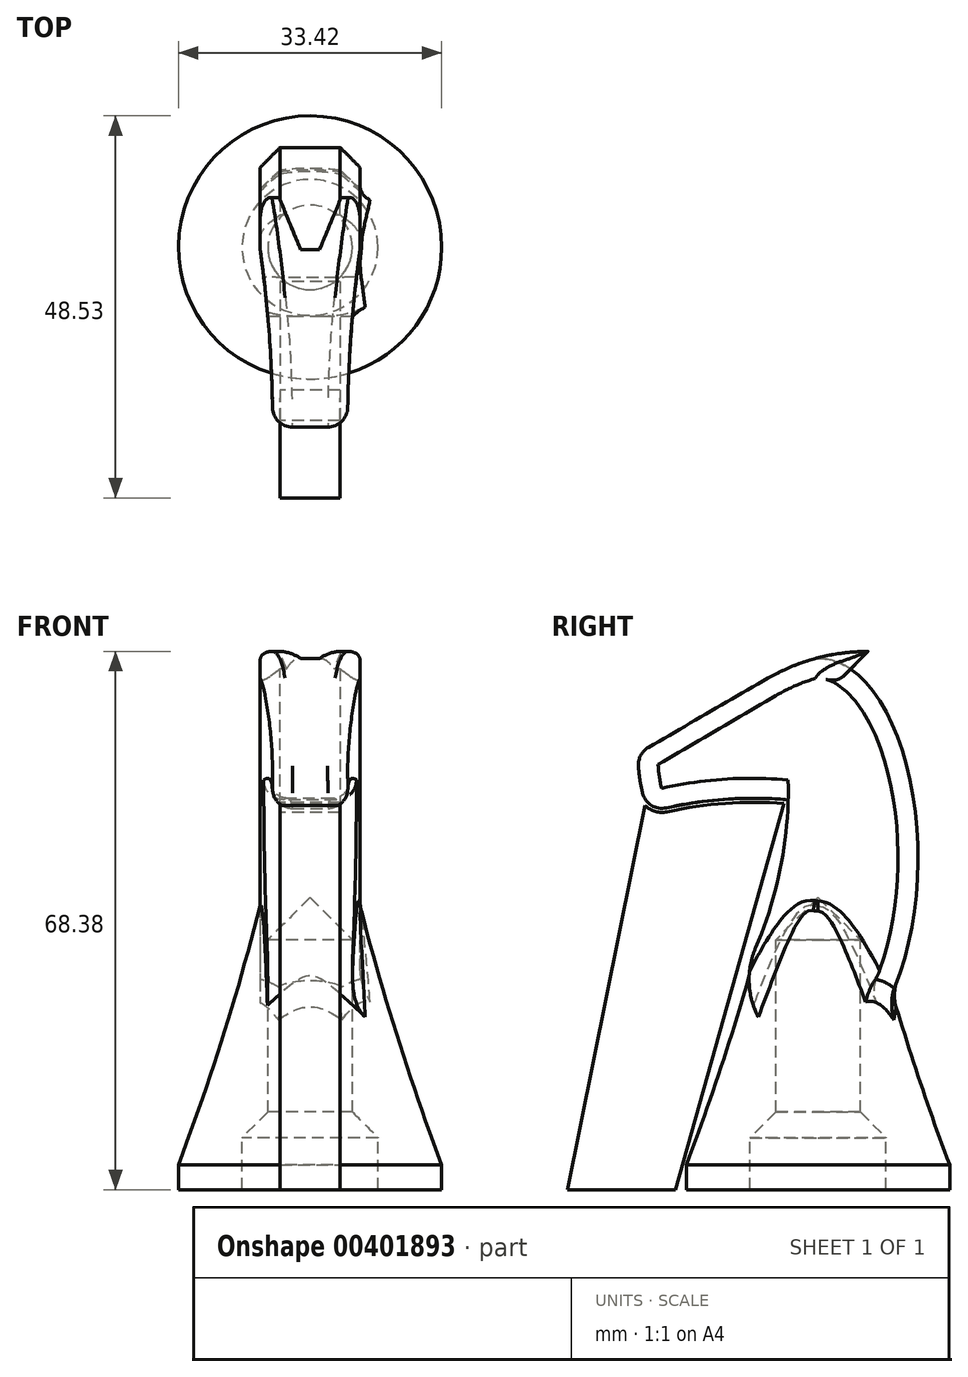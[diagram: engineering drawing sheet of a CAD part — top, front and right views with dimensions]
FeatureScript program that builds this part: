
annotation { "Feature Type Name" : "Feature", "Feature Type Description" : "" }
export const myFeature = defineFeature(function(context is Context, id is Id, definition is map)
    precondition{}
    {
        {
            var Q0;
            Q0=qCreatedBy(makeId("Right.planeOp"),FACE);
            var sketch = newSketch(context, id + "F0", { "sketchPlane" : qUnion([Q0])});
            skArc(sketch, "E0", {"start": v(6.35, 68.38) * mm, "mid": v(-0.22, 67.51) * mm, "end": v(-6.35, 64.97) * mm});
            skLineSegment(sketch, "E1.bottom", {"start": v(-16.71, 68.38) * mm, "end": v(16.71, 68.38) * mm, "construction": true});
            skLineSegment(sketch, "E1.top", {"start": v(-16.71, 0) * mm, "end": v(16.71, 0) * mm, "construction": true});
            skLineSegment(sketch, "E1.left", {"start": v(-16.71, 68.38) * mm, "end": v(-16.71, 0) * mm, "construction": true});
            skLineSegment(sketch, "E1.right", {"start": v(16.71, 68.38) * mm, "end": v(16.71, 0) * mm, "construction": true});
            skArc(sketch, "E2", {"start": v(-22.85, 55.45) * mm, "mid": v(-22.57, 51.63) * mm, "end": v(-21.52, 47.94) * mm});
            skLineSegment(sketch, "E3", {"start": v(-22.85, 55.45) * mm, "end": v(-6.35, 64.97) * mm});
            skLineSegment(sketch, "E4", {"start": v(-3.8, 54.94) * mm, "end": v(-22.57, 51.63) * mm, "construction": true});
            skLineSegment(sketch, "E5", {"start": v(6.35, 68.38) * mm, "end": v(4.1, 66.13) * mm});
            skArc(sketch, "E6", {"start": v(-3.8, 49.53) * mm, "mid": v(-12.74, 49.52) * mm, "end": v(-21.52, 47.94) * mm});
            skArc(sketch, "E7", {"start": v(-7.94, 30.7) * mm, "mid": v(-4.97, 39.92) * mm, "end": v(-3.81, 49.53) * mm});
            skEllipticalArc(sketch, "E8", {});
            skPoint(sketch, "E9.visualSharp", {"position": v(-10, 26.46) * mm});
            skArc(sketch, "E9.filletArc", {"start": v(-7.94, 30.7) * mm, "mid": v(-7.62, 21.98) * mm, "end": v(-0.66, 16.73) * mm});
            const initialGuessF0  = {"E8": [0, 0.04209513881585966, 0, 1, 0.0254, 0.0127, 3.089740436383142, 5.954051655491451]};
            skSetInitialGuess(sketch, initialGuessF0);
            skSolve(sketch);
        }
        {
            var Q0;
            Q0 = qSketchRegion(id + "F0", true);
            extrude(context, id + "F1", {"entities" : qUnion([Q0]), "depth" : 12.7 * mm, "symmetric" : true});
        }
        {
            var Q0;
            Q0=qCreatedBy(makeId("Top.planeOp"),FACE);
            var sketch = newSketch(context, id + "F2", { "sketchPlane" : qUnion([Q0])});
            skCircle(sketch, "E10", {"center": v(166.76, -22.85) * mm, "radius": 162 * mm});
            skLineSegment(sketch, "E11", {"start": v(0, 0) * mm, "end": v(0, 17.42) * mm, "construction": true});
            skCircle(sketch, "E12.MirrorC", {"center": v(-166.76, -22.85) * mm, "radius": 162 * mm});
            skSolve(sketch);
        }
        {
            var Q0;
            Q0 = qSketchRegion(id + "F2", true);
            extrude(context, id + "F3", {"entities" : qUnion([Q0]), "operationType" : NewBodyOperationType.REMOVE, "endBound" : BoundingType.THROUGH_ALL, "depth" : 25.4 * mm});
        }
        {
            var Q0;
            Q0=qCreatedBy(makeId("Right.planeOp"),FACE);
            var sketch = newSketch(context, id + "F4", { "sketchPlane" : qUnion([Q0])});
            skLineSegment(sketch, "E13", {"start": v(-8.64, 0) * mm, "end": v(-16.71, 0) * mm});
            skLineSegment(sketch, "E14", {"start": v(-16.71, 0) * mm, "end": v(-16.71, 3.17) * mm});
            skArc(sketch, "E15", {"start": v(-16.71, 3.17) * mm, "mid": v(-6.63, 34.92) * mm, "end": v(0, 67.57) * mm});
            skLineSegment(sketch, "E16", {"start": v(0, 67.57) * mm, "end": v(0, 37.12) * mm});
            skLineSegment(sketch, "E17", {"start": v(0, 37.12) * mm, "end": v(-5.37, 31.75) * mm});
            skLineSegment(sketch, "E18", {"start": v(-5.37, 31.75) * mm, "end": v(-5.37, 9.87) * mm});
            skLineSegment(sketch, "E19", {"start": v(-5.37, 9.87) * mm, "end": v(-8.64, 6.6) * mm});
            skLineSegment(sketch, "E20", {"start": v(-8.64, 6.6) * mm, "end": v(-8.64, 0) * mm});
            skSolve(sketch);
        }
        {
            var Q0;
            Q0 = qSketchRegion(id + "F4", true);
            var Q1;
            Q1=sQuery(id+"F4.wireOp",EDGE,"E16");
            revolve(context, id + "F5", {"operationType" : NewBodyOperationType.ADD, "entities" : qUnion([Q0]), "axis" : qUnion([Q1]), "revolveType" : RevolveType.FULL});
        }
        {
            var Q0;
            Q0=qCreatedBy(makeId("Right.planeOp"),FACE);
            var sketch = newSketch(context, id + "F6", { "sketchPlane" : qUnion([Q0])});
            skArc(sketch, "E21.0", {"start": v(-7.94, 30.7) * mm, "mid": v(-4.97, 39.92) * mm, "end": v(-3.81, 49.53) * mm});
            skLineSegment(sketch, "E22", {"start": v(-3.81, 49.53) * mm, "end": v(-15.99, 40.42) * mm});
            skLineSegment(sketch, "E23", {"start": v(-15.99, 40.42) * mm, "end": v(-7.94, 30.7) * mm});
            skSolve(sketch);
        }
        {
            var Q0;
            Q0 = qSketchRegion(id + "F6", true);
            extrude(context, id + "F7", {"entities" : qUnion([Q0]), "operationType" : NewBodyOperationType.REMOVE, "oppositeDirection" : true, "depth" : 25.4 * mm, "symmetric" : true});
        }
        {
            var Q0;
            Q0=qCreatedBy(makeId("Right.planeOp"),FACE);
            var sketch = newSketch(context, id + "F8", { "sketchPlane" : qUnion([Q0])});
            skLineSegment(sketch, "E24.0", {"start": v(0, 37.12) * mm, "end": v(-5.37, 31.75) * mm});
            skLineSegment(sketch, "E24.1", {"start": v(-5.37, 31.75) * mm, "end": v(-5.37, 9.87) * mm});
            skLineSegment(sketch, "E24.2", {"start": v(-5.37, 9.87) * mm, "end": v(-8.64, 6.6) * mm});
            skLineSegment(sketch, "E24.3", {"start": v(-8.64, 6.6) * mm, "end": v(-8.64, 0) * mm});
            skLineSegment(sketch, "E25", {"start": v(-8.64, 0) * mm, "end": v(0, 0) * mm});
            skLineSegment(sketch, "E26", {"start": v(0, 0) * mm, "end": v(0, 37.12) * mm});
            skSolve(sketch);
        }
        {
            var Q0;
            Q0 = qSketchRegion(id + "F8", true);
            var Q1;
            Q1=sQuery(id+"F8.wireOp",EDGE,"E26");
            revolve(context, id + "F9", {"operationType" : NewBodyOperationType.REMOVE, "entities" : qUnion([Q0]), "axis" : qUnion([Q1]), "revolveType" : RevolveType.FULL, "oppositeDirection" : true});
        }
        {
            var Q0;
            Q0=makeQuery(id+"F3.boolean.opBoolean","INTERSECT",EDGE,{"derivedFrom":[makeQuery(id+"F1.opExtrude","SWEPT_FACE",FACE,{"disambiguationData":[OSD([sQuery(id+"F0.wireOp",EDGE,"E3")])]}),makeQuery(id+"F3.opExtrude","SWEPT_FACE",FACE,{"disambiguationData":[OSD([sQuery(id+"F2.wireOp",EDGE,"E10")])]})]});
            var Q1;
            Q1=makeQuery(id+"F3.boolean.opBoolean","INTERSECT",EDGE,{"derivedFrom":[makeQuery(id+"F1.opExtrude","SWEPT_FACE",FACE,{"disambiguationData":[OSD([sQuery(id+"F0.wireOp",EDGE,"E6")])]}),makeQuery(id+"F3.opExtrude","SWEPT_FACE",FACE,{"disambiguationData":[OSD([sQuery(id+"F2.wireOp",EDGE,"E10")])]})]});
            var Q2;
            Q2=makeQuery(id+"F3.boolean.opBoolean","INTERSECT",EDGE,{"derivedFrom":[makeQuery(id+"F1.opExtrude","SWEPT_FACE",FACE,{"disambiguationData":[OSD([sQuery(id+"F0.wireOp",EDGE,"E3")])]}),makeQuery(id+"F3.opExtrude","SWEPT_FACE",FACE,{"disambiguationData":[OSD([sQuery(id+"F2.wireOp",EDGE,"E12.MirrorC")])]})]});
            var Q3;
            Q3=makeQuery(id+"F3.boolean.opBoolean","INTERSECT",EDGE,{"derivedFrom":[makeQuery(id+"F1.opExtrude","SWEPT_FACE",FACE,{"disambiguationData":[OSD([sQuery(id+"F0.wireOp",EDGE,"E6")])]}),makeQuery(id+"F3.opExtrude","SWEPT_FACE",FACE,{"disambiguationData":[OSD([sQuery(id+"F2.wireOp",EDGE,"E12.MirrorC")])]})]});
            var Q4;
            Q4=makeQuery(id+"F3.boolean.opBoolean","INTERSECT",EDGE,{"derivedFrom":[makeQuery(id+"F1.opExtrude","SWEPT_FACE",FACE,{"disambiguationData":[OSD([sQuery(id+"F0.wireOp",EDGE,"E7")])]}),makeQuery(id+"F3.opExtrude","SWEPT_FACE",FACE,{"disambiguationData":[OSD([sQuery(id+"F2.wireOp",EDGE,"E12.MirrorC")])]})]});
            var Q5;
            Q5=makeQuery(id+"F3.boolean.opBoolean","INTERSECT",EDGE,{"derivedFrom":[makeQuery(id+"F1.opExtrude","SWEPT_FACE",FACE,{"disambiguationData":[OSD([sQuery(id+"F0.wireOp",EDGE,"E7")])]}),makeQuery(id+"F3.opExtrude","SWEPT_FACE",FACE,{"disambiguationData":[OSD([sQuery(id+"F2.wireOp",EDGE,"E10")])]})]});
            var Q6;
            Q6=makeQuery(id+"F1.opExtrude","SWEPT_FACE",FACE,{"disambiguationData":[OSD([sQuery(id+"F0.wireOp",EDGE,"E2")])]});
            var Q7;
            Q7=makeQuery(id+"F3.boolean.opBoolean","INTERSECT",EDGE,{"derivedFrom":[makeQuery(id+"F1.opExtrude","CAP_FACE",FACE,{"disambiguationData":[OSD([sQuery(id+"F0.wireOp",EDGE,"E0"),sQuery(id+"F0.wireOp",EDGE,"E2"),sQuery(id+"F0.wireOp",EDGE,"E3"),sQuery(id+"F0.wireOp",EDGE,"E5"),sQuery(id+"F0.wireOp",EDGE,"E6"),sQuery(id+"F0.wireOp",EDGE,"E7"),sQuery(id+"F0.wireOp",EDGE,"E8"),sQuery(id+"F0.wireOp",EDGE,"E9.filletArc")])],"isStart":false}),makeQuery(id+"F3.opExtrude","SWEPT_FACE",FACE,{"disambiguationData":[OSD([sQuery(id+"F2.wireOp",EDGE,"E10")])]})]});
            var Q8;
            Q8=makeQuery(id+"F3.boolean.opBoolean","INTERSECT",EDGE,{"derivedFrom":[makeQuery(id+"F1.opExtrude","CAP_FACE",FACE,{"disambiguationData":[OSD([sQuery(id+"F0.wireOp",EDGE,"E0"),sQuery(id+"F0.wireOp",EDGE,"E2"),sQuery(id+"F0.wireOp",EDGE,"E3"),sQuery(id+"F0.wireOp",EDGE,"E5"),sQuery(id+"F0.wireOp",EDGE,"E6"),sQuery(id+"F0.wireOp",EDGE,"E7"),sQuery(id+"F0.wireOp",EDGE,"E8"),sQuery(id+"F0.wireOp",EDGE,"E9.filletArc")])],"isStart":true}),makeQuery(id+"F3.opExtrude","SWEPT_FACE",FACE,{"disambiguationData":[OSD([sQuery(id+"F2.wireOp",EDGE,"E12.MirrorC")])]})]});
            fillet(context, id + "F10", {"entities" : qUnion([Q0, Q1, Q2, Q3, Q4, Q5, Q6, Q7, Q8]), "radius" : 2.54 * mm, "tangentPropagation" : true, "allowEdgeOverflow" : false});
        }
        {
            var Q0;
            Q0=makeQuery(id+"F1.opExtrude","CAP_EDGE",EDGE,{"disambiguationData":[OSD([sQuery(id+"F0.wireOp",EDGE,"E8")])],"isStart":false});
            var Q1;
            Q1=makeQuery(id+"F1.opExtrude","CAP_EDGE",EDGE,{"disambiguationData":[OSD([sQuery(id+"F0.wireOp",EDGE,"E8")])],"isStart":true});
            chamfer(context, id + "F11", {"entities" : qUnion([Q0, Q1]), "width" : 2.54 * mm, "tangentPropagation" : true});
        }
        {
            var Q0;
            Q0=makeQuery(id+"F1.opExtrude","CAP_EDGE",EDGE,{"disambiguationData":[OSD([sQuery(id+"F0.wireOp",EDGE,"E5")])],"isStart":false});
            var Q1;
            Q1=makeQuery(id+"F1.opExtrude","CAP_EDGE",EDGE,{"disambiguationData":[OSD([sQuery(id+"F0.wireOp",EDGE,"E5")])],"isStart":true});
            fillet(context, id + "F12", {"entities" : qUnion([Q0, Q1]), "radius" : 1.27 * mm, "allowEdgeOverflow" : false});
        }
        {
            var Q0;
            Q0=makeQuery(id+"F5.boolean.opBoolean","INTERSECT",EDGE,{"derivedFrom":[makeQuery(id+"F1.opExtrude","CAP_FACE",FACE,{"disambiguationData":[OSD([sQuery(id+"F0.wireOp",EDGE,"E0"),sQuery(id+"F0.wireOp",EDGE,"E2"),sQuery(id+"F0.wireOp",EDGE,"E3"),sQuery(id+"F0.wireOp",EDGE,"E5"),sQuery(id+"F0.wireOp",EDGE,"E6"),sQuery(id+"F0.wireOp",EDGE,"E7"),sQuery(id+"F0.wireOp",EDGE,"E8"),sQuery(id+"F0.wireOp",EDGE,"E9.filletArc")])],"isStart":false}),makeQuery(id+"F5.opRevolve","SWEPT_FACE",FACE,{"disambiguationData":[OSD([sQuery(id+"F4.wireOp",EDGE,"E15")])]})]});
            var Q1;
            {var subQ1=sQuery(id+"F0.wireOp",EDGE,"E8");Q1=makeQuery(id+"F11.opChamfer","BLEND_EDGE",EDGE,{"blendedFrom":[makeQuery(id+"F1.opExtrude","CAP_EDGE",EDGE,{"disambiguationData":[OSD([subQ1])],"isStart":false}),makeQuery(id+"F5.boolean.opBoolean","SPLIT",FACE,{"disambiguationData":[TD([makeQuery(id+"F1.opExtrude","SWEPT_FACE",FACE,{"disambiguationData":[OSD([subQ1])]})])],"derivedFrom":makeQuery(id+"F5.opRevolve","SWEPT_FACE",FACE,{"disambiguationData":[OSD([sQuery(id+"F4.wireOp",EDGE,"E15")])]})})],"blendedInto":[makeQuery(id+"F5.boolean.opBoolean","SPLIT",FACE,{"disambiguationData":[TD([makeQuery(id+"F1.opExtrude","SWEPT_FACE",FACE,{"disambiguationData":[OSD([subQ1])]})])],"derivedFrom":makeQuery(id+"F5.opRevolve","SWEPT_FACE",FACE,{"disambiguationData":[OSD([sQuery(id+"F4.wireOp",EDGE,"E15")])]})})]});}
            var Q2;
            Q2=makeQuery(id+"F5.boolean.opBoolean","INTERSECT",EDGE,{"derivedFrom":[makeQuery(id+"F1.opExtrude","SWEPT_FACE",FACE,{"disambiguationData":[OSD([sQuery(id+"F0.wireOp",EDGE,"E8")])]}),makeQuery(id+"F5.opRevolve","SWEPT_FACE",FACE,{"disambiguationData":[OSD([sQuery(id+"F4.wireOp",EDGE,"E15")])]})]});
            var Q3;
            {var subQ1=sQuery(id+"F0.wireOp",EDGE,"E8");Q3=makeQuery(id+"F11.opChamfer","BLEND_EDGE",EDGE,{"blendedFrom":[makeQuery(id+"F1.opExtrude","CAP_EDGE",EDGE,{"disambiguationData":[OSD([subQ1])],"isStart":true}),makeQuery(id+"F5.boolean.opBoolean","SPLIT",FACE,{"disambiguationData":[TD([makeQuery(id+"F1.opExtrude","SWEPT_FACE",FACE,{"disambiguationData":[OSD([subQ1])]})])],"derivedFrom":makeQuery(id+"F5.opRevolve","SWEPT_FACE",FACE,{"disambiguationData":[OSD([sQuery(id+"F4.wireOp",EDGE,"E15")])]})})],"blendedInto":[makeQuery(id+"F5.boolean.opBoolean","SPLIT",FACE,{"disambiguationData":[TD([makeQuery(id+"F1.opExtrude","SWEPT_FACE",FACE,{"disambiguationData":[OSD([subQ1])]})])],"derivedFrom":makeQuery(id+"F5.opRevolve","SWEPT_FACE",FACE,{"disambiguationData":[OSD([sQuery(id+"F4.wireOp",EDGE,"E15")])]})})]});}
            fillet(context, id + "F13", {"entities" : qUnion([Q0, Q1, Q2, Q3]), "radius" : 5.08 * mm, "tangentPropagation" : true, "allowEdgeOverflow" : false});
        }
        {
            var Q0;
            Q0=qCreatedBy(makeId("Top.planeOp"),FACE);
            cPlane(context, id + "F14", {"entities" : qUnion([Q0]), "cplaneType" : CPlaneType.OFFSET, "offset" : 76.2 * mm, "width" : 152.4 * mm, "height" : 152.4 * mm});
        }
        {
            var Q0;
            Q0=qCreatedBy(id+"F14.planeOp",FACE);
            var sketch = newSketch(context, id + "F15", { "sketchPlane" : qUnion([Q0])});
            skLineSegment(sketch, "E27", {"start": v(0, -3.18) * mm, "end": v(4.3, 7.22) * mm});
            skLineSegment(sketch, "E28", {"start": v(4.3, 7.22) * mm, "end": v(-4.3, 7.22) * mm});
            skLineSegment(sketch, "E29", {"start": v(-4.3, 7.22) * mm, "end": v(0, -3.18) * mm});
            skLineSegment(sketch, "E30", {"start": v(0, 0) * mm, "end": v(0, 9.74) * mm, "construction": true});
            skPoint(sketch, "E30.endSnap0", {"position": v(0, 7.22) * mm});
            skSolve(sketch);
        }
        {
            var Q0;
            Q0 = qSketchRegion(id + "F15", true);
            var Q1;
            {var subQ1=sQuery(id+"F0.wireOp",EDGE,"E8");var subQ4=sQuery(id+"F0.wireOp",EDGE,"E5");Q1=makeQuery(id+"F5.boolean.opBoolean","SPLIT",FACE,{"disambiguationData":[TD([makeQuery(id+"F1.opExtrude","SWEPT_FACE",FACE,{"disambiguationData":[OSD([subQ4])]})])],"derivedFrom":makeQuery(id+"F1.opExtrude","SWEPT_FACE",FACE,{"disambiguationData":[OSD([subQ1])]})});}
            extrude(context, id + "F16", {"entities" : qUnion([Q0]), "operationType" : NewBodyOperationType.REMOVE, "endBound" : BoundingType.UP_TO_SURFACE, "oppositeDirection" : true, "endBoundEntityFace" : qUnion([Q1]), "depth" : 25.4 * mm});
        }
        {
            var Q0;
            Q0=qCreatedBy(makeId("Right.planeOp"),FACE);
            var sketch = newSketch(context, id + "F17", { "sketchPlane" : qUnion([Q0])});
            skArc(sketch, "E31.0", {"start": v(-19.17, 48) * mm, "mid": v(-11.78, 49.09) * mm, "end": v(-4.32, 49.06) * mm});
            skLineSegment(sketch, "E32", {"start": v(-4.32, 49.06) * mm, "end": v(-18.14, 0) * mm});
            skLineSegment(sketch, "E33", {"start": v(-18.14, 0) * mm, "end": v(-31.82, 0) * mm});
            skLineSegment(sketch, "E34", {"start": v(-31.82, 0) * mm, "end": v(-21.97, 48.8) * mm});
            skArc(sketch, "E35.0", {"start": v(-21.97, 48.8) * mm, "mid": v(-20.67, 48.05) * mm, "end": v(-19.17, 48) * mm});
            skPoint(sketch, "E36", {"position": v(-16.71, 3.17) * mm});
            skSolve(sketch);
        }
        {
            var Q0;
            Q0 = qSketchRegion(id + "F17", true);
            extrude(context, id + "F18", {"entities" : qUnion([Q0]), "depth" : 7.62 * mm, "symmetric" : true});
        }
    });
